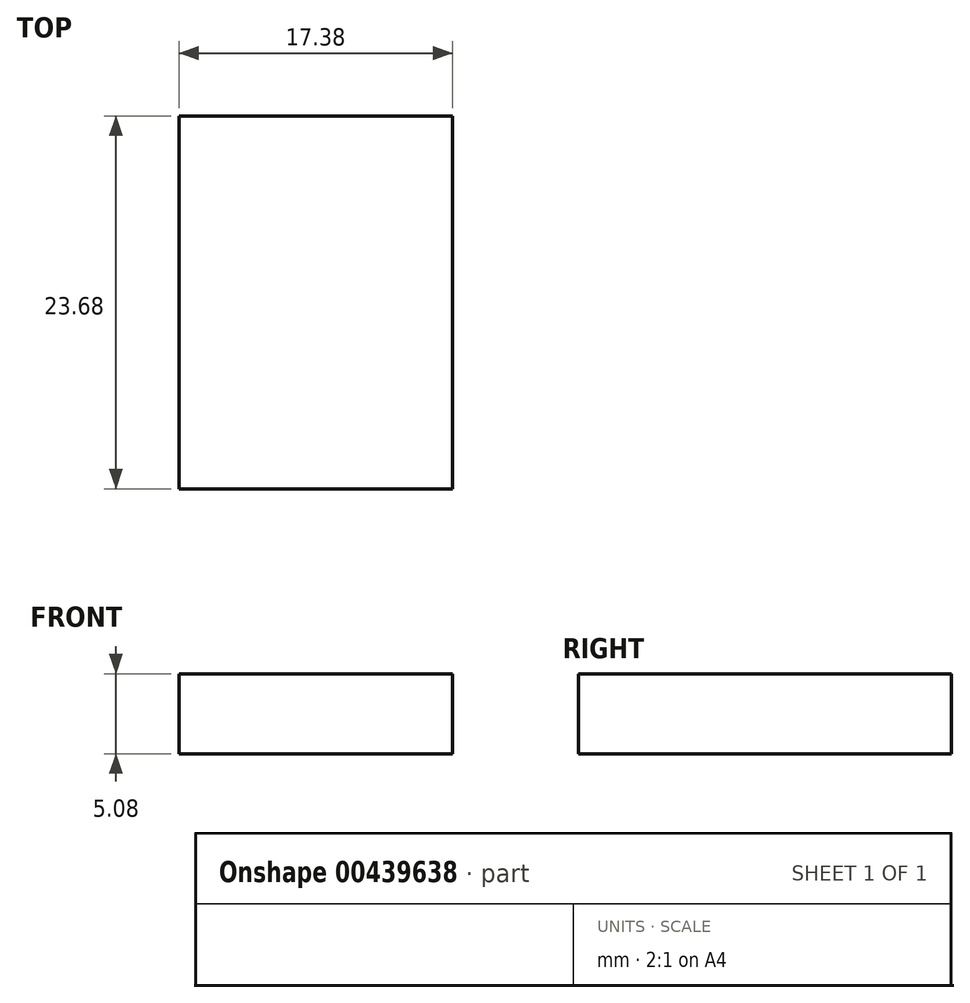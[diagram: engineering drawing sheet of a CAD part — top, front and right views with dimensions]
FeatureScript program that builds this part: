
annotation { "Feature Type Name" : "Feature", "Feature Type Description" : "" }
export const myFeature = defineFeature(function(context is Context, id is Id, definition is map)
    precondition{}
    {
        {
            var Q0;
            Q0=qCreatedBy(makeId("Top.planeOp"),FACE);
            var sketch = newSketch(context, id + "F0", { "sketchPlane" : qUnion([Q0])});
            skLineSegment(sketch, "E0.bottom", {"start": v(-46.02, 35.33) * mm, "end": v(-28.64, 35.33) * mm});
            skLineSegment(sketch, "E0.top", {"start": v(-46.02, 11.65) * mm, "end": v(-28.64, 11.65) * mm});
            skLineSegment(sketch, "E0.left", {"start": v(-46.02, 35.33) * mm, "end": v(-46.02, 11.65) * mm});
            skLineSegment(sketch, "E0.right", {"start": v(-28.64, 35.33) * mm, "end": v(-28.64, 11.65) * mm});
            skSolve(sketch);
        }
        {
            var Q0;
            Q0 = qSketchRegion(id + "F0", true);
            extrude(context, id + "F1", {"entities" : qUnion([Q0]), "depth" : 5.08 * mm});
        }
    });
